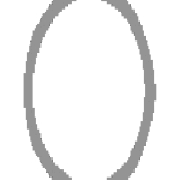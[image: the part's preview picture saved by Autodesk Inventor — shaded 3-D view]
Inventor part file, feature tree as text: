
AUTODESK INVENTOR PART (.ipt)
format: ipt  version: 2021 (Build 250183000, 183)  size: 111,616 bytes
history: native  units: in
note: dims shown in document units (in); Inventor stores cm internally (conversion verified against a paired STEP export)
features: other x4, sketch x3, plane x1
ambient origin geometry x8: Origin, YZ Plane, XZ Plane, XY Plane, X Axis, Y Axis, Z Axis, Center Point
bodies: Solid1 (feature_tree), Body (feature_tree)
feature tree (8):
  other  "Driven Length"
  other  "Frame Generator"
  other  "Start Plane"
  other  "End Plane"
  sketch  "Sketch"  dims[d2=28.1877in d4=-0.0in d5=28.1877in d6=0.12in d7=0.0in d8=90.0deg d9=28.1877in]
  sketch  "Sketch2"  dims[d0=1.0in]
  plane  "Work Plane3"
  sketch  "Sketch3"  dims[d1=0.065in]
